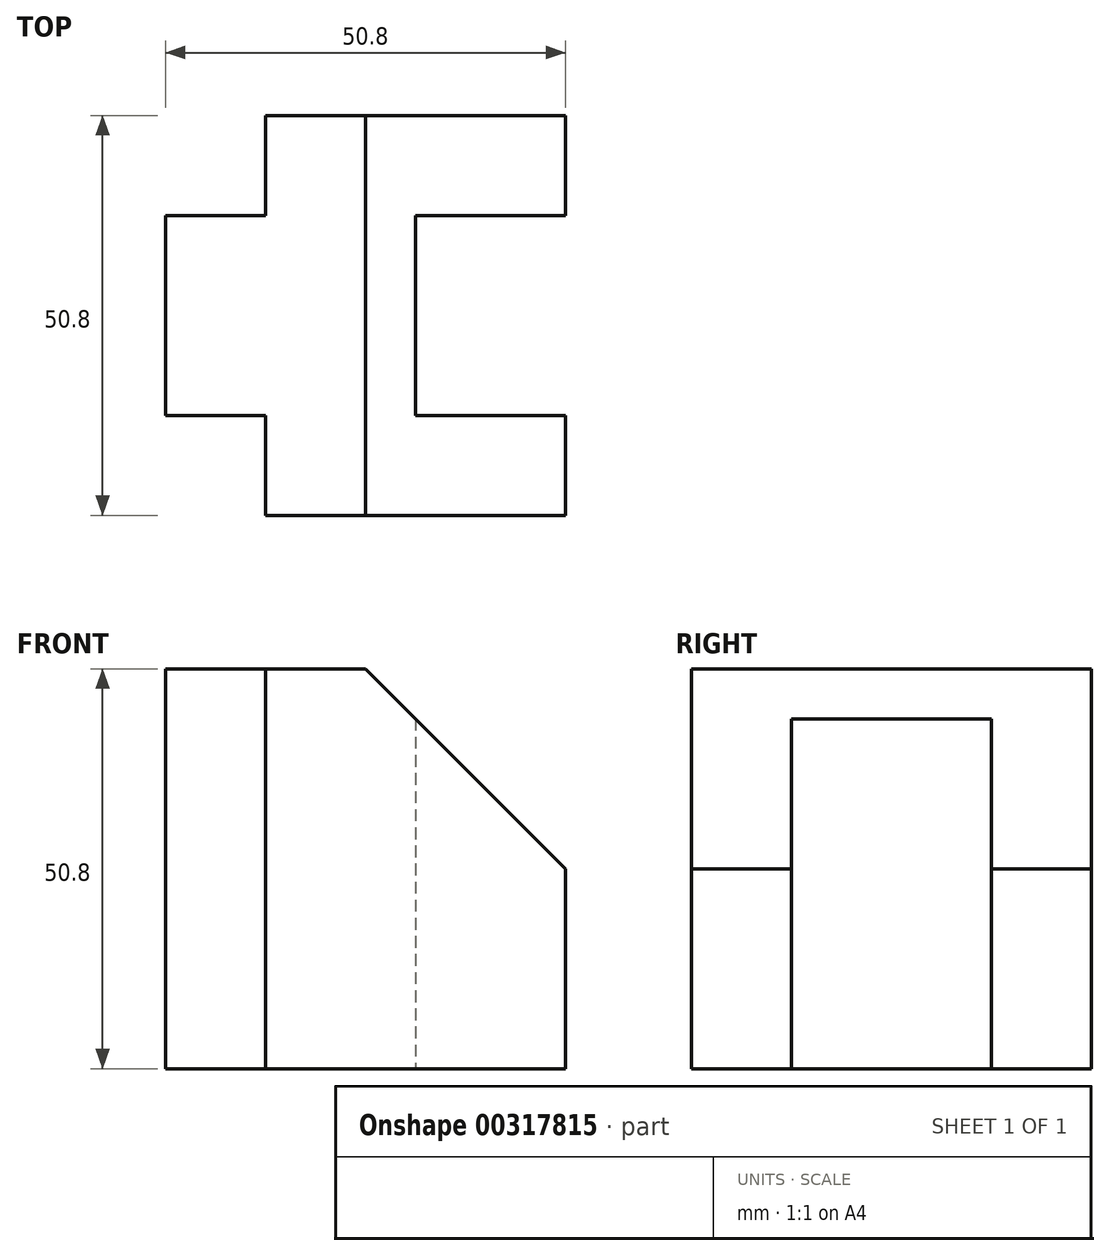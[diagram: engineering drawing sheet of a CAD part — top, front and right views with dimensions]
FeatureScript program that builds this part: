
annotation { "Feature Type Name" : "Feature", "Feature Type Description" : "" }
export const myFeature = defineFeature(function(context is Context, id is Id, definition is map)
    precondition{}
    {
        {
            var Q0;
            Q0=qCreatedBy(makeId("Top.planeOp"),FACE);
            var sketch = newSketch(context, id + "F0", { "sketchPlane" : qUnion([Q0])});
            skLineSegment(sketch, "E0", {"start": v(0, 0) * mm, "end": v(-12.7, 0) * mm});
            skLineSegment(sketch, "E1", {"start": v(-12.7, 0) * mm, "end": v(-12.7, 12.7) * mm});
            skLineSegment(sketch, "E2", {"start": v(-12.7, 12.7) * mm, "end": v(-25.4, 12.7) * mm});
            skLineSegment(sketch, "E3", {"start": v(-25.4, 12.7) * mm, "end": v(-25.4, 38.1) * mm});
            skLineSegment(sketch, "E4", {"start": v(-25.4, 38.1) * mm, "end": v(-12.7, 38.1) * mm});
            skLineSegment(sketch, "E5", {"start": v(-12.7, 38.1) * mm, "end": v(-12.7, 50.8) * mm});
            skLineSegment(sketch, "E6", {"start": v(-12.7, 50.8) * mm, "end": v(0, 50.8) * mm});
            skLineSegment(sketch, "E7", {"start": v(0, 50.8) * mm, "end": v(0, 0) * mm});
            skLineSegment(sketch, "E8", {"start": v(0, 0) * mm, "end": v(25.4, 0) * mm});
            skLineSegment(sketch, "E9", {"start": v(25.4, 0) * mm, "end": v(25.4, 12.7) * mm});
            skLineSegment(sketch, "E10", {"start": v(25.4, 12.7) * mm, "end": v(6.35, 12.7) * mm});
            skLineSegment(sketch, "E11", {"start": v(6.35, 12.7) * mm, "end": v(6.35, 38.1) * mm});
            skLineSegment(sketch, "E12", {"start": v(6.35, 38.1) * mm, "end": v(25.4, 38.1) * mm});
            skLineSegment(sketch, "E13", {"start": v(25.4, 38.1) * mm, "end": v(25.4, 50.8) * mm});
            skLineSegment(sketch, "E14", {"start": v(25.4, 50.8) * mm, "end": v(0, 50.8) * mm});
            skSolve(sketch);
        }
        {
            var Q0;
            Q0 = qSketchRegion(id + "F0", true);
            extrude(context, id + "F1", {"entities" : qUnion([Q0]), "depth" : 50.8 * mm});
        }
        {
            var Q0;
            Q0=qCreatedBy(makeId("Front.planeOp"),FACE);
            var sketch = newSketch(context, id + "F2", { "sketchPlane" : qUnion([Q0])});
            skLineSegment(sketch, "E15", {"start": v(0, 50.8) * mm, "end": v(25.4, 50.8) * mm});
            skLineSegment(sketch, "E16", {"start": v(25.4, 50.8) * mm, "end": v(25.4, 25.4) * mm});
            skLineSegment(sketch, "E17", {"start": v(25.4, 25.4) * mm, "end": v(0, 50.8) * mm});
            skSolve(sketch);
        }
        {
            var Q0;
            Q0 = qSketchRegion(id + "F2", true);
            extrude(context, id + "F3", {"entities" : qUnion([Q0]), "operationType" : NewBodyOperationType.REMOVE, "endBound" : BoundingType.THROUGH_ALL, "oppositeDirection" : true, "depth" : 25.4 * mm});
        }
    });
